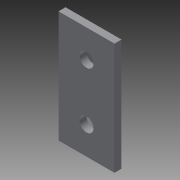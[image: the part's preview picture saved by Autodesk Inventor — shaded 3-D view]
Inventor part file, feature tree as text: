
AUTODESK INVENTOR PART (.ipt)
format: ipt  version: 2014 (Build 180170000, 170)  size: 81,408 bytes
history: native  units: in
note: dims shown in document units (in); Inventor stores cm internally (conversion verified against a paired STEP export)
features: sketch x2, extrude x1, hole x1
ambient origin geometry x8: Origin, YZ Plane, XZ Plane, XY Plane, X Axis, Y Axis, Z Axis, Center Point
bodies: Solid1 (feature_tree)
feature tree (4):
  extrude  "Extrusion1"  Depth=2.0in
  hole  "Hole1"  [1 undecoded]
  sketch  "Sketch1"  dims[d0=1.0in d1=2.0in]
  sketch  "Sketch2"  dims[d2=0.125in d3=0.0in d4=0.5in d5=0.5in d6=0.25in d7=0.75in d8=0.375in d9=0.25in d10=0.5635in d11=1.0in d12=0.8108in]
note: 1 required parameter value undecoded (feature->parameter linkage not recoverable at this tier; creation-order binding heuristic only, values carry confidence <= 0.55)
